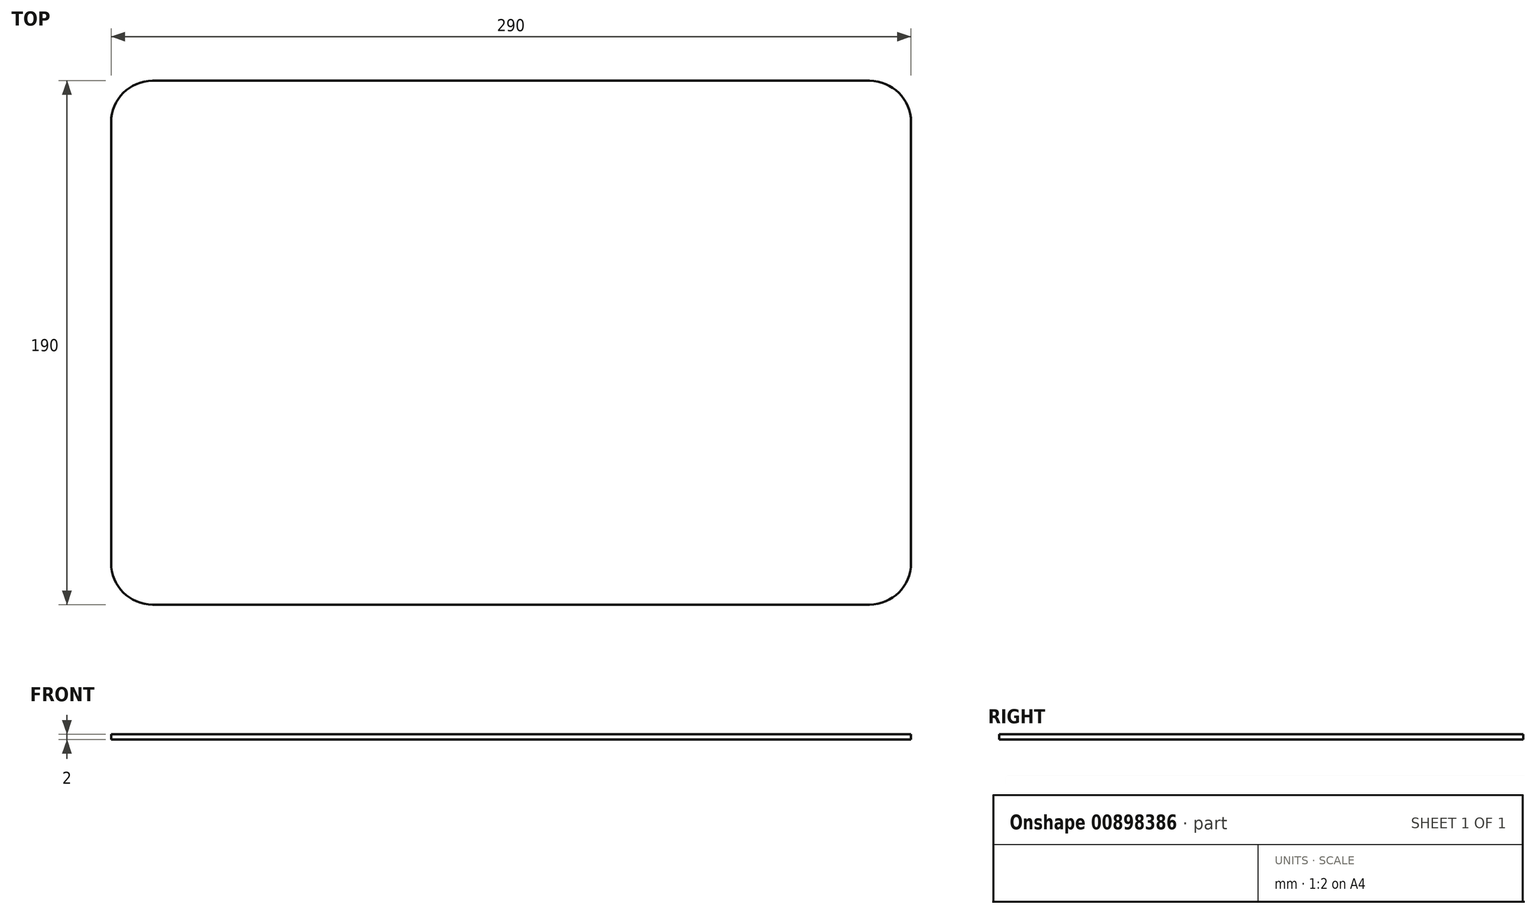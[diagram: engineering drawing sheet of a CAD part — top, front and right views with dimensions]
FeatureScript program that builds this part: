
annotation { "Feature Type Name" : "Feature", "Feature Type Description" : "" }
export const myFeature = defineFeature(function(context is Context, id is Id, definition is map)
    precondition{}
    {
        {
            var Q0;
            Q0=qCreatedBy(makeId("Top.planeOp"),FACE);
            var sketch = newSketch(context, id + "F0", { "sketchPlane" : qUnion([Q0])});
            skLineSegment(sketch, "E0.bottom", {"start": v(-135, -95) * mm, "end": v(135, -95) * mm});
            skLineSegment(sketch, "E0.top", {"start": v(-130, 95) * mm, "end": v(135, 95) * mm});
            skLineSegment(sketch, "E0.left", {"start": v(-145, -85.71) * mm, "end": v(-145, 80) * mm});
            skLineSegment(sketch, "E0.right", {"start": v(145, -85.71) * mm, "end": v(145, 84.29) * mm});
            skPoint(sketch, "E0.middle", {"position": v(0, 0) * mm});
            skPoint(sketch, "E1.visualSharp", {"position": v(-145, 95) * mm});
            skPoint(sketch, "E2.visualSharp", {"position": v(145, 95) * mm});
            skPoint(sketch, "E3.visualSharp", {"position": v(145, -95) * mm});
            skPoint(sketch, "E4.visualSharp", {"position": v(-145, -95) * mm});
            skLineSegment(sketch, "E5.bottom", {"start": v(-94, 35) * mm, "end": v(-130, 35) * mm});
            skLineSegment(sketch, "E5.top", {"start": v(-94, 85) * mm, "end": v(-130, 85) * mm});
            skLineSegment(sketch, "E5.left", {"start": v(-89, 40) * mm, "end": v(-89, 80) * mm});
            skLineSegment(sketch, "E5.right", {"start": v(-135, 40) * mm, "end": v(-135, 80) * mm});
            skPoint(sketch, "E5.middle", {"position": v(-112, 60) * mm});
            skPoint(sketch, "E6.visualSharp", {"position": v(-135, 85) * mm});
            skArc(sketch, "E6.filletArc", {"start": v(-130, 85) * mm, "mid": v(-133.54, 83.54) * mm, "end": v(-135, 80) * mm});
            skPoint(sketch, "E7.visualSharp", {"position": v(-89, 85) * mm});
            skArc(sketch, "E7.filletArc", {"start": v(-89, 80) * mm, "mid": v(-90.46, 83.54) * mm, "end": v(-94, 85) * mm});
            skPoint(sketch, "E8.visualSharp", {"position": v(-89, 35) * mm});
            skArc(sketch, "E8.filletArc", {"start": v(-94, 35) * mm, "mid": v(-90.46, 36.46) * mm, "end": v(-89, 40) * mm});
            skPoint(sketch, "E9.visualSharp", {"position": v(-135, 35) * mm});
            skArc(sketch, "E9.filletArc", {"start": v(-135, 40) * mm, "mid": v(-133.54, 36.46) * mm, "end": v(-130, 35) * mm});
            skArc(sketch, "E10.0", {"start": v(-130, 95) * mm, "mid": v(-140.6, 90.6) * mm, "end": v(-145, 80) * mm});
            skLineSegment(sketch, "E11", {"start": v(0, 0) * mm, "end": v(0, 193.58) * mm, "construction": true});
            skArc(sketch, "E12.MirrorCS", {"start": v(130, 95) * mm, "mid": v(140.6, 90.6) * mm, "end": v(145, 80) * mm});
            skLineSegment(sketch, "E13", {"start": v(0, 0) * mm, "end": v(78.7, 0) * mm, "construction": true});
            skArc(sketch, "E14.MirrorCS", {"start": v(-130, -95) * mm, "mid": v(-140.6, -90.6) * mm, "end": v(-145, -80) * mm});
            skArc(sketch, "E15.MirrorCS", {"start": v(130, -95) * mm, "mid": v(140.6, -90.6) * mm, "end": v(145, -80) * mm});
            skArc(sketch, "E16.0.1.0", {"start": v(-130, 25) * mm, "mid": v(-133.54, 23.54) * mm, "end": v(-135, 20) * mm});
            skLineSegment(sketch, "E16.0.1.1", {"start": v(-94, 25) * mm, "end": v(-130, 25) * mm});
            skArc(sketch, "E16.0.1.2", {"start": v(-89, 20) * mm, "mid": v(-90.46, 23.54) * mm, "end": v(-94, 25) * mm});
            skLineSegment(sketch, "E16.0.1.3", {"start": v(-89, -20) * mm, "end": v(-89, 20) * mm});
            skArc(sketch, "E16.0.1.4", {"start": v(-94, -25) * mm, "mid": v(-90.46, -23.54) * mm, "end": v(-89, -20) * mm});
            skLineSegment(sketch, "E16.0.1.5", {"start": v(-94, -25) * mm, "end": v(-130, -25) * mm});
            skArc(sketch, "E16.0.1.6", {"start": v(-135, -20) * mm, "mid": v(-133.54, -23.54) * mm, "end": v(-130, -25) * mm});
            skLineSegment(sketch, "E16.0.1.7", {"start": v(-135, -20) * mm, "end": v(-135, 20) * mm});
            skArc(sketch, "E16.0.2.0", {"start": v(-130, -35) * mm, "mid": v(-133.54, -36.46) * mm, "end": v(-135, -40) * mm});
            skLineSegment(sketch, "E16.0.2.1", {"start": v(-94, -35) * mm, "end": v(-130, -35) * mm});
            skArc(sketch, "E16.0.2.2", {"start": v(-89, -40) * mm, "mid": v(-90.46, -36.46) * mm, "end": v(-94, -35) * mm});
            skLineSegment(sketch, "E16.0.2.3", {"start": v(-89, -80) * mm, "end": v(-89, -40) * mm});
            skArc(sketch, "E16.0.2.4", {"start": v(-94, -85) * mm, "mid": v(-90.46, -83.54) * mm, "end": v(-89, -80) * mm});
            skLineSegment(sketch, "E16.0.2.5", {"start": v(-94, -85) * mm, "end": v(-130, -85) * mm});
            skArc(sketch, "E16.0.2.6", {"start": v(-135, -80) * mm, "mid": v(-133.54, -83.54) * mm, "end": v(-130, -85) * mm});
            skLineSegment(sketch, "E16.0.2.7", {"start": v(-135, -80) * mm, "end": v(-135, -40) * mm});
            skArc(sketch, "E16.1.0.0", {"start": v(-74, 85) * mm, "mid": v(-77.54, 83.54) * mm, "end": v(-79, 80) * mm});
            skLineSegment(sketch, "E16.1.0.1", {"start": v(-38, 85) * mm, "end": v(-74, 85) * mm});
            skArc(sketch, "E16.1.0.2", {"start": v(-33, 80) * mm, "mid": v(-34.46, 83.54) * mm, "end": v(-38, 85) * mm});
            skLineSegment(sketch, "E16.1.0.3", {"start": v(-33, 40) * mm, "end": v(-33, 80) * mm});
            skArc(sketch, "E16.1.0.4", {"start": v(-38, 35) * mm, "mid": v(-34.46, 36.46) * mm, "end": v(-33, 40) * mm});
            skLineSegment(sketch, "E16.1.0.5", {"start": v(-38, 35) * mm, "end": v(-74, 35) * mm});
            skArc(sketch, "E16.1.0.6", {"start": v(-79, 40) * mm, "mid": v(-77.54, 36.46) * mm, "end": v(-74, 35) * mm});
            skLineSegment(sketch, "E16.1.0.7", {"start": v(-79, 40) * mm, "end": v(-79, 80) * mm});
            skArc(sketch, "E16.1.1.0", {"start": v(-74, 25) * mm, "mid": v(-77.54, 23.54) * mm, "end": v(-79, 20) * mm});
            skLineSegment(sketch, "E16.1.1.1", {"start": v(-38, 25) * mm, "end": v(-74, 25) * mm});
            skArc(sketch, "E16.1.1.2", {"start": v(-33, 20) * mm, "mid": v(-34.46, 23.54) * mm, "end": v(-38, 25) * mm});
            skLineSegment(sketch, "E16.1.1.3", {"start": v(-33, -20) * mm, "end": v(-33, 20) * mm});
            skArc(sketch, "E16.1.1.4", {"start": v(-38, -25) * mm, "mid": v(-34.46, -23.54) * mm, "end": v(-33, -20) * mm});
            skLineSegment(sketch, "E16.1.1.5", {"start": v(-38, -25) * mm, "end": v(-74, -25) * mm});
            skArc(sketch, "E16.1.1.6", {"start": v(-79, -20) * mm, "mid": v(-77.54, -23.54) * mm, "end": v(-74, -25) * mm});
            skLineSegment(sketch, "E16.1.1.7", {"start": v(-79, -20) * mm, "end": v(-79, 20) * mm});
            skArc(sketch, "E16.1.2.0", {"start": v(-74, -35) * mm, "mid": v(-77.54, -36.46) * mm, "end": v(-79, -40) * mm});
            skLineSegment(sketch, "E16.1.2.1", {"start": v(-38, -35) * mm, "end": v(-74, -35) * mm});
            skArc(sketch, "E16.1.2.2", {"start": v(-33, -40) * mm, "mid": v(-34.46, -36.46) * mm, "end": v(-38, -35) * mm});
            skLineSegment(sketch, "E16.1.2.3", {"start": v(-33, -80) * mm, "end": v(-33, -40) * mm});
            skArc(sketch, "E16.1.2.4", {"start": v(-38, -85) * mm, "mid": v(-34.46, -83.54) * mm, "end": v(-33, -80) * mm});
            skLineSegment(sketch, "E16.1.2.5", {"start": v(-38, -85) * mm, "end": v(-74, -85) * mm});
            skArc(sketch, "E16.1.2.6", {"start": v(-79, -80) * mm, "mid": v(-77.54, -83.54) * mm, "end": v(-74, -85) * mm});
            skLineSegment(sketch, "E16.1.2.7", {"start": v(-79, -80) * mm, "end": v(-79, -40) * mm});
            skArc(sketch, "E16.2.0.0", {"start": v(-18, 85) * mm, "mid": v(-21.54, 83.54) * mm, "end": v(-23, 80) * mm});
            skLineSegment(sketch, "E16.2.0.1", {"start": v(18, 85) * mm, "end": v(-18, 85) * mm});
            skArc(sketch, "E16.2.0.2", {"start": v(23, 80) * mm, "mid": v(21.54, 83.54) * mm, "end": v(18, 85) * mm});
            skLineSegment(sketch, "E16.2.0.3", {"start": v(23, 40) * mm, "end": v(23, 80) * mm});
            skArc(sketch, "E16.2.0.4", {"start": v(18, 35) * mm, "mid": v(21.54, 36.46) * mm, "end": v(23, 40) * mm});
            skLineSegment(sketch, "E16.2.0.5", {"start": v(18, 35) * mm, "end": v(-18, 35) * mm});
            skArc(sketch, "E16.2.0.6", {"start": v(-23, 40) * mm, "mid": v(-21.54, 36.46) * mm, "end": v(-18, 35) * mm});
            skLineSegment(sketch, "E16.2.0.7", {"start": v(-23, 40) * mm, "end": v(-23, 80) * mm});
            skArc(sketch, "E16.2.1.0", {"start": v(-18, 25) * mm, "mid": v(-21.54, 23.54) * mm, "end": v(-23, 20) * mm});
            skLineSegment(sketch, "E16.2.1.1", {"start": v(18, 25) * mm, "end": v(-18, 25) * mm});
            skArc(sketch, "E16.2.1.2", {"start": v(23, 20) * mm, "mid": v(21.54, 23.54) * mm, "end": v(18, 25) * mm});
            skLineSegment(sketch, "E16.2.1.3", {"start": v(23, -20) * mm, "end": v(23, 20) * mm});
            skArc(sketch, "E16.2.1.4", {"start": v(18, -25) * mm, "mid": v(21.54, -23.54) * mm, "end": v(23, -20) * mm});
            skLineSegment(sketch, "E16.2.1.5", {"start": v(18, -25) * mm, "end": v(-18, -25) * mm});
            skArc(sketch, "E16.2.1.6", {"start": v(-23, -20) * mm, "mid": v(-21.54, -23.54) * mm, "end": v(-18, -25) * mm});
            skLineSegment(sketch, "E16.2.1.7", {"start": v(-23, -20) * mm, "end": v(-23, 20) * mm});
            skArc(sketch, "E16.2.2.0", {"start": v(-18, -35) * mm, "mid": v(-21.54, -36.46) * mm, "end": v(-23, -40) * mm});
            skLineSegment(sketch, "E16.2.2.1", {"start": v(18, -35) * mm, "end": v(-18, -35) * mm});
            skArc(sketch, "E16.2.2.2", {"start": v(23, -40) * mm, "mid": v(21.54, -36.46) * mm, "end": v(18, -35) * mm});
            skLineSegment(sketch, "E16.2.2.3", {"start": v(23, -80) * mm, "end": v(23, -40) * mm});
            skArc(sketch, "E16.2.2.4", {"start": v(18, -85) * mm, "mid": v(21.54, -83.54) * mm, "end": v(23, -80) * mm});
            skLineSegment(sketch, "E16.2.2.5", {"start": v(18, -85) * mm, "end": v(-18, -85) * mm});
            skArc(sketch, "E16.2.2.6", {"start": v(-23, -80) * mm, "mid": v(-21.54, -83.54) * mm, "end": v(-18, -85) * mm});
            skLineSegment(sketch, "E16.2.2.7", {"start": v(-23, -80) * mm, "end": v(-23, -40) * mm});
            skArc(sketch, "E16.3.0.0", {"start": v(38, 85) * mm, "mid": v(34.46, 83.54) * mm, "end": v(33, 80) * mm});
            skLineSegment(sketch, "E16.3.0.1", {"start": v(74, 85) * mm, "end": v(38, 85) * mm});
            skArc(sketch, "E16.3.0.2", {"start": v(79, 80) * mm, "mid": v(77.54, 83.54) * mm, "end": v(74, 85) * mm});
            skLineSegment(sketch, "E16.3.0.3", {"start": v(79, 40) * mm, "end": v(79, 80) * mm});
            skArc(sketch, "E16.3.0.4", {"start": v(74, 35) * mm, "mid": v(77.54, 36.46) * mm, "end": v(79, 40) * mm});
            skLineSegment(sketch, "E16.3.0.5", {"start": v(74, 35) * mm, "end": v(38, 35) * mm});
            skArc(sketch, "E16.3.0.6", {"start": v(33, 40) * mm, "mid": v(34.46, 36.46) * mm, "end": v(38, 35) * mm});
            skLineSegment(sketch, "E16.3.0.7", {"start": v(33, 40) * mm, "end": v(33, 80) * mm});
            skArc(sketch, "E16.3.1.0", {"start": v(38, 25) * mm, "mid": v(34.46, 23.54) * mm, "end": v(33, 20) * mm});
            skLineSegment(sketch, "E16.3.1.1", {"start": v(74, 25) * mm, "end": v(38, 25) * mm});
            skArc(sketch, "E16.3.1.2", {"start": v(79, 20) * mm, "mid": v(77.54, 23.54) * mm, "end": v(74, 25) * mm});
            skLineSegment(sketch, "E16.3.1.3", {"start": v(79, -20) * mm, "end": v(79, 20) * mm});
            skArc(sketch, "E16.3.1.4", {"start": v(74, -25) * mm, "mid": v(77.54, -23.54) * mm, "end": v(79, -20) * mm});
            skLineSegment(sketch, "E16.3.1.5", {"start": v(74, -25) * mm, "end": v(38, -25) * mm});
            skArc(sketch, "E16.3.1.6", {"start": v(33, -20) * mm, "mid": v(34.46, -23.54) * mm, "end": v(38, -25) * mm});
            skLineSegment(sketch, "E16.3.1.7", {"start": v(33, -20) * mm, "end": v(33, 20) * mm});
            skArc(sketch, "E16.3.2.0", {"start": v(38, -35) * mm, "mid": v(34.46, -36.46) * mm, "end": v(33, -40) * mm});
            skLineSegment(sketch, "E16.3.2.1", {"start": v(74, -35) * mm, "end": v(38, -35) * mm});
            skArc(sketch, "E16.3.2.2", {"start": v(79, -40) * mm, "mid": v(77.54, -36.46) * mm, "end": v(74, -35) * mm});
            skLineSegment(sketch, "E16.3.2.3", {"start": v(79, -80) * mm, "end": v(79, -40) * mm});
            skArc(sketch, "E16.3.2.4", {"start": v(74, -85) * mm, "mid": v(77.54, -83.54) * mm, "end": v(79, -80) * mm});
            skLineSegment(sketch, "E16.3.2.5", {"start": v(74, -85) * mm, "end": v(38, -85) * mm});
            skArc(sketch, "E16.3.2.6", {"start": v(33, -80) * mm, "mid": v(34.46, -83.54) * mm, "end": v(38, -85) * mm});
            skLineSegment(sketch, "E16.3.2.7", {"start": v(33, -80) * mm, "end": v(33, -40) * mm});
            skArc(sketch, "E16.4.0.0", {"start": v(94, 85) * mm, "mid": v(90.46, 83.54) * mm, "end": v(89, 80) * mm});
            skLineSegment(sketch, "E16.4.0.1", {"start": v(130, 85) * mm, "end": v(94, 85) * mm});
            skArc(sketch, "E16.4.0.2", {"start": v(135, 80) * mm, "mid": v(133.54, 83.54) * mm, "end": v(130, 85) * mm});
            skLineSegment(sketch, "E16.4.0.3", {"start": v(135, 40) * mm, "end": v(135, 80) * mm});
            skArc(sketch, "E16.4.0.4", {"start": v(130, 35) * mm, "mid": v(133.54, 36.46) * mm, "end": v(135, 40) * mm});
            skLineSegment(sketch, "E16.4.0.5", {"start": v(130, 35) * mm, "end": v(94, 35) * mm});
            skArc(sketch, "E16.4.0.6", {"start": v(89, 40) * mm, "mid": v(90.46, 36.46) * mm, "end": v(94, 35) * mm});
            skLineSegment(sketch, "E16.4.0.7", {"start": v(89, 40) * mm, "end": v(89, 80) * mm});
            skArc(sketch, "E16.4.1.0", {"start": v(94, 25) * mm, "mid": v(90.46, 23.54) * mm, "end": v(89, 20) * mm});
            skLineSegment(sketch, "E16.4.1.1", {"start": v(130, 25) * mm, "end": v(94, 25) * mm});
            skArc(sketch, "E16.4.1.2", {"start": v(135, 20) * mm, "mid": v(133.54, 23.54) * mm, "end": v(130, 25) * mm});
            skLineSegment(sketch, "E16.4.1.3", {"start": v(135, -20) * mm, "end": v(135, 20) * mm});
            skArc(sketch, "E16.4.1.4", {"start": v(130, -25) * mm, "mid": v(133.54, -23.54) * mm, "end": v(135, -20) * mm});
            skLineSegment(sketch, "E16.4.1.5", {"start": v(130, -25) * mm, "end": v(94, -25) * mm});
            skArc(sketch, "E16.4.1.6", {"start": v(89, -20) * mm, "mid": v(90.46, -23.54) * mm, "end": v(94, -25) * mm});
            skLineSegment(sketch, "E16.4.1.7", {"start": v(89, -20) * mm, "end": v(89, 20) * mm});
            skArc(sketch, "E16.4.2.0", {"start": v(94, -35) * mm, "mid": v(90.46, -36.46) * mm, "end": v(89, -40) * mm});
            skLineSegment(sketch, "E16.4.2.1", {"start": v(130, -35) * mm, "end": v(94, -35) * mm});
            skArc(sketch, "E16.4.2.2", {"start": v(135, -40) * mm, "mid": v(133.54, -36.46) * mm, "end": v(130, -35) * mm});
            skLineSegment(sketch, "E16.4.2.3", {"start": v(135, -80) * mm, "end": v(135, -40) * mm});
            skArc(sketch, "E16.4.2.4", {"start": v(130, -85) * mm, "mid": v(133.54, -83.54) * mm, "end": v(135, -80) * mm});
            skLineSegment(sketch, "E16.4.2.5", {"start": v(130, -85) * mm, "end": v(94, -85) * mm});
            skArc(sketch, "E16.4.2.6", {"start": v(89, -80) * mm, "mid": v(90.46, -83.54) * mm, "end": v(94, -85) * mm});
            skLineSegment(sketch, "E16.4.2.7", {"start": v(89, -80) * mm, "end": v(89, -40) * mm});
            skLineSegment(sketch, "E16.direction1", {"start": v(-130, 35) * mm, "end": v(-74, 35) * mm, "construction": true});
            skLineSegment(sketch, "E16.direction2", {"start": v(-130, 35) * mm, "end": v(-130, -25) * mm, "construction": true});
            skSolve(sketch);
        }
        {
            var Q0;
            Q0=makeQuery(id+"F0.imprint","IMPRINT",FACE,{"disambiguationData":[TD([[makeQuery(id+"F0.imprint","IMPRINT",EDGE,{"derivedFrom":sQuery(id+"F0.wireOp",EDGE,"E5.bottom")}),1.0]])]});
            var Q1;
            Q1=makeQuery(id+"F0.imprint","IMPRINT",FACE,{"disambiguationData":[TD([[makeQuery(id+"F0.imprint","IMPRINT",EDGE,{"derivedFrom":sQuery(id+"F0.wireOp",EDGE,"E16.4.2.0")}),1.0]])]});
            var Q2;
            Q2=makeQuery(id+"F0.imprint","IMPRINT",FACE,{"disambiguationData":[TD([[makeQuery(id+"F0.imprint","IMPRINT",EDGE,{"derivedFrom":sQuery(id+"F0.wireOp",EDGE,"E16.3.2.0")}),1.0]])]});
            var Q3;
            Q3=makeQuery(id+"F0.imprint","IMPRINT",FACE,{"disambiguationData":[TD([[makeQuery(id+"F0.imprint","IMPRINT",EDGE,{"derivedFrom":sQuery(id+"F0.wireOp",EDGE,"E16.4.1.0")}),1.0]])]});
            var Q4;
            Q4=makeQuery(id+"F0.imprint","IMPRINT",FACE,{"disambiguationData":[TD([[makeQuery(id+"F0.imprint","IMPRINT",EDGE,{"derivedFrom":sQuery(id+"F0.wireOp",EDGE,"E16.3.1.0")}),1.0]])]});
            var Q5;
            Q5=makeQuery(id+"F0.imprint","IMPRINT",FACE,{"disambiguationData":[TD([[makeQuery(id+"F0.imprint","IMPRINT",EDGE,{"derivedFrom":sQuery(id+"F0.wireOp",EDGE,"E16.4.0.0")}),1.0]])]});
            var Q6;
            Q6=makeQuery(id+"F0.imprint","IMPRINT",FACE,{"disambiguationData":[TD([[makeQuery(id+"F0.imprint","IMPRINT",EDGE,{"derivedFrom":sQuery(id+"F0.wireOp",EDGE,"E16.3.0.0")}),1.0]])]});
            var Q7;
            Q7=makeQuery(id+"F0.imprint","IMPRINT",FACE,{"disambiguationData":[TD([[makeQuery(id+"F0.imprint","IMPRINT",EDGE,{"derivedFrom":sQuery(id+"F0.wireOp",EDGE,"E16.2.0.0")}),1.0]])]});
            var Q8;
            Q8=makeQuery(id+"F0.imprint","IMPRINT",FACE,{"disambiguationData":[TD([[makeQuery(id+"F0.imprint","IMPRINT",EDGE,{"derivedFrom":sQuery(id+"F0.wireOp",EDGE,"E16.2.1.0")}),1.0]])]});
            var Q9;
            Q9=makeQuery(id+"F0.imprint","IMPRINT",FACE,{"disambiguationData":[TD([[makeQuery(id+"F0.imprint","IMPRINT",EDGE,{"derivedFrom":sQuery(id+"F0.wireOp",EDGE,"E16.1.2.0")}),1.0]])]});
            var Q10;
            Q10=makeQuery(id+"F0.imprint","IMPRINT",FACE,{"disambiguationData":[TD([[makeQuery(id+"F0.imprint","IMPRINT",EDGE,{"derivedFrom":sQuery(id+"F0.wireOp",EDGE,"E16.1.1.0")}),1.0]])]});
            var Q11;
            Q11=makeQuery(id+"F0.imprint","IMPRINT",FACE,{"disambiguationData":[TD([[makeQuery(id+"F0.imprint","IMPRINT",EDGE,{"derivedFrom":sQuery(id+"F0.wireOp",EDGE,"E16.1.0.0")}),1.0]])]});
            var Q12;
            Q12=makeQuery(id+"F0.imprint","IMPRINT",FACE,{"disambiguationData":[TD([[makeQuery(id+"F0.imprint","IMPRINT",EDGE,{"derivedFrom":sQuery(id+"F0.wireOp",EDGE,"E5.bottom")}),-1.0]])]});
            var Q13;
            Q13=makeQuery(id+"F0.imprint","IMPRINT",FACE,{"disambiguationData":[TD([[makeQuery(id+"F0.imprint","IMPRINT",EDGE,{"derivedFrom":sQuery(id+"F0.wireOp",EDGE,"E16.0.1.0")}),1.0]])]});
            var Q14;
            Q14=makeQuery(id+"F0.imprint","IMPRINT",FACE,{"disambiguationData":[TD([[makeQuery(id+"F0.imprint","IMPRINT",EDGE,{"derivedFrom":sQuery(id+"F0.wireOp",EDGE,"E16.0.2.0")}),1.0]])]});
            var Q15;
            Q15=makeQuery(id+"F0.imprint","IMPRINT",FACE,{"disambiguationData":[TD([[makeQuery(id+"F0.imprint","IMPRINT",EDGE,{"derivedFrom":sQuery(id+"F0.wireOp",EDGE,"E16.2.2.0")}),1.0]])]});
            extrude(context, id + "F1", {"entities" : qUnion([Q0, Q1, Q2, Q3, Q4, Q5, Q6, Q7, Q8, Q9, Q10, Q11, Q12, Q13, Q14, Q15]), "depth" : 2 * mm, "offsetDistance" : 25 * mm});
        }
    });
